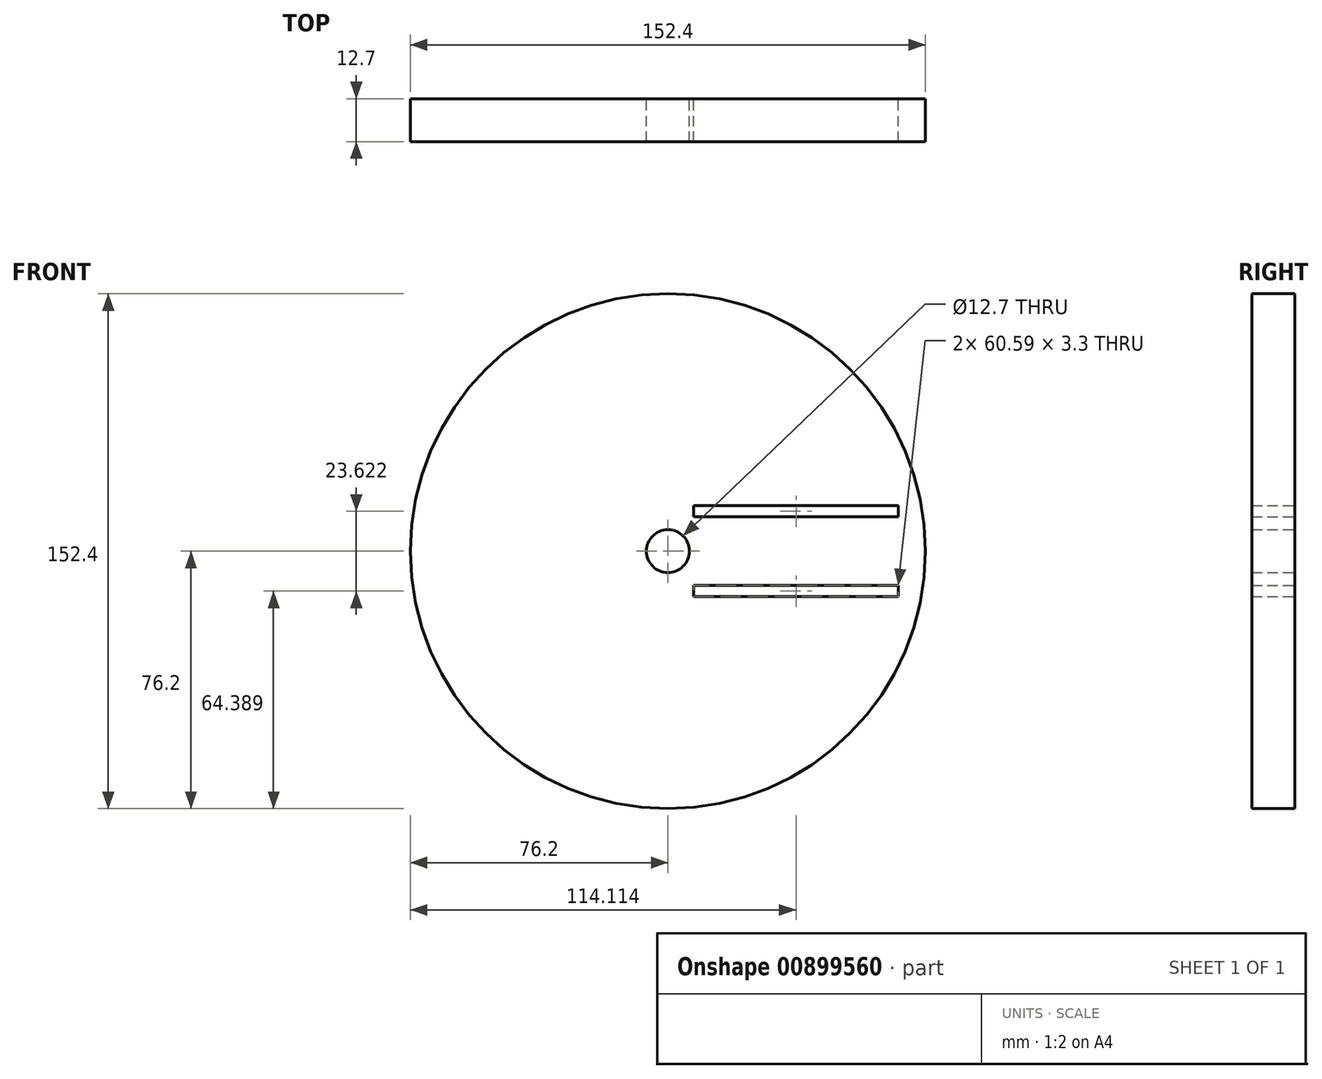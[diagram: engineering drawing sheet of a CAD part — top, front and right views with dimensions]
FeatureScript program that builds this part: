
annotation { "Feature Type Name" : "Feature", "Feature Type Description" : "" }
export const myFeature = defineFeature(function(context is Context, id is Id, definition is map)
    precondition{}
    {
        {
            var Q0;
            Q0=qCreatedBy(makeId("Front.planeOp"),FACE);
            var sketch = newSketch(context, id + "F0", { "sketchPlane" : qUnion([Q0])});
            skCircle(sketch, "E0", {"center": v(0, 0) * mm, "radius": 76.2 * mm});
            skCircle(sketch, "E1", {"center": v(0, 0) * mm, "radius": 6.35 * mm});
            skLineSegment(sketch, "E2.bottom", {"start": v(7.62, 1.65) * mm, "end": v(68.58, 1.65) * mm});
            skLineSegment(sketch, "E2.top", {"start": v(7.62, -1.65) * mm, "end": v(68.58, -1.65) * mm});
            skLineSegment(sketch, "E2.left", {"start": v(7.62, 1.65) * mm, "end": v(7.62, -1.65) * mm});
            skLineSegment(sketch, "E2.right", {"start": v(68.58, 1.65) * mm, "end": v(68.58, -1.65) * mm});
            skPoint(sketch, "E2.middle", {"position": v(38.1, 0) * mm});
            skLineSegment(sketch, "E3.bottom", {"start": v(0, 0) * mm, "end": v(7.62, 0) * mm});
            skLineSegment(sketch, "E3.top", {"start": v(0, 10.16) * mm, "end": v(7.62, 10.16) * mm});
            skLineSegment(sketch, "E3.left", {"start": v(0, 0) * mm, "end": v(0, 10.16) * mm});
            skLineSegment(sketch, "E3.right", {"start": v(7.62, 0) * mm, "end": v(7.62, 10.16) * mm});
            skLineSegment(sketch, "E4.bottom", {"start": v(7.62, 0) * mm, "end": v(0, 0) * mm});
            skLineSegment(sketch, "E4.top", {"start": v(7.62, -10.16) * mm, "end": v(0, -10.16) * mm});
            skLineSegment(sketch, "E4.left", {"start": v(7.62, 0) * mm, "end": v(7.62, -10.16) * mm});
            skLineSegment(sketch, "E4.right", {"start": v(0, 0) * mm, "end": v(0, -10.16) * mm});
            skLineSegment(sketch, "E5.bottom", {"start": v(7.62, 10.16) * mm, "end": v(68.2, 10.16) * mm});
            skLineSegment(sketch, "E5.top", {"start": v(7.62, 13.46) * mm, "end": v(68.2, 13.46) * mm});
            skLineSegment(sketch, "E5.left", {"start": v(7.62, 10.16) * mm, "end": v(7.62, 13.46) * mm});
            skLineSegment(sketch, "E5.right", {"start": v(68.2, 10.16) * mm, "end": v(68.2, 13.46) * mm});
            skLineSegment(sketch, "E6.bottom", {"start": v(7.62, -10.16) * mm, "end": v(68.2, -10.16) * mm});
            skLineSegment(sketch, "E6.top", {"start": v(7.62, -13.46) * mm, "end": v(68.2, -13.46) * mm});
            skLineSegment(sketch, "E6.left", {"start": v(7.62, -10.16) * mm, "end": v(7.62, -13.46) * mm});
            skLineSegment(sketch, "E6.right", {"start": v(68.2, -10.16) * mm, "end": v(68.2, -13.46) * mm});
            skSolve(sketch);
        }
        {
            var Q0;
            Q0=makeQuery(id+"F0.imprint","IMPRINT",FACE,{"disambiguationData":[TD([[makeQuery(id+"F0.imprint","IMPRINT",EDGE,{"derivedFrom":sQuery(id+"F0.wireOp",EDGE,"E0")}),1.0]])]});
            var Q1;
            {var subQ5=sQuery(id+"F0.wireOp",EDGE,"E3.top");Q1=makeQuery(id+"F0.imprint","IMPRINT",FACE,{"disambiguationData":[TD([[makeQuery(id+"F0.imprint","IMPRINT",EDGE,{"derivedFrom":subQ5}),-1.0]])]});}
            var Q2;
            {var subQ4=sQuery(id+"F0.wireOp",EDGE,"E4.top");Q2=makeQuery(id+"F0.imprint","IMPRINT",FACE,{"disambiguationData":[TD([[makeQuery(id+"F0.imprint","IMPRINT",EDGE,{"derivedFrom":subQ4}),-1.0]])]});}
            var Q3;
            {var subQ1=sQuery(id+"F0.wireOp",EDGE,"E2.bottom");Q3=makeQuery(id+"F0.imprint","IMPRINT",FACE,{"disambiguationData":[TD([[makeQuery(id+"F0.imprint","IMPRINT",EDGE,{"derivedFrom":subQ1}),-1.0]])]});}
            extrude(context, id + "F1", {"entities" : qUnion([Q0, Q1, Q2, Q3]), "depth" : 12.7 * mm, "offsetDistance" : 25.4 * mm});
        }
    });
